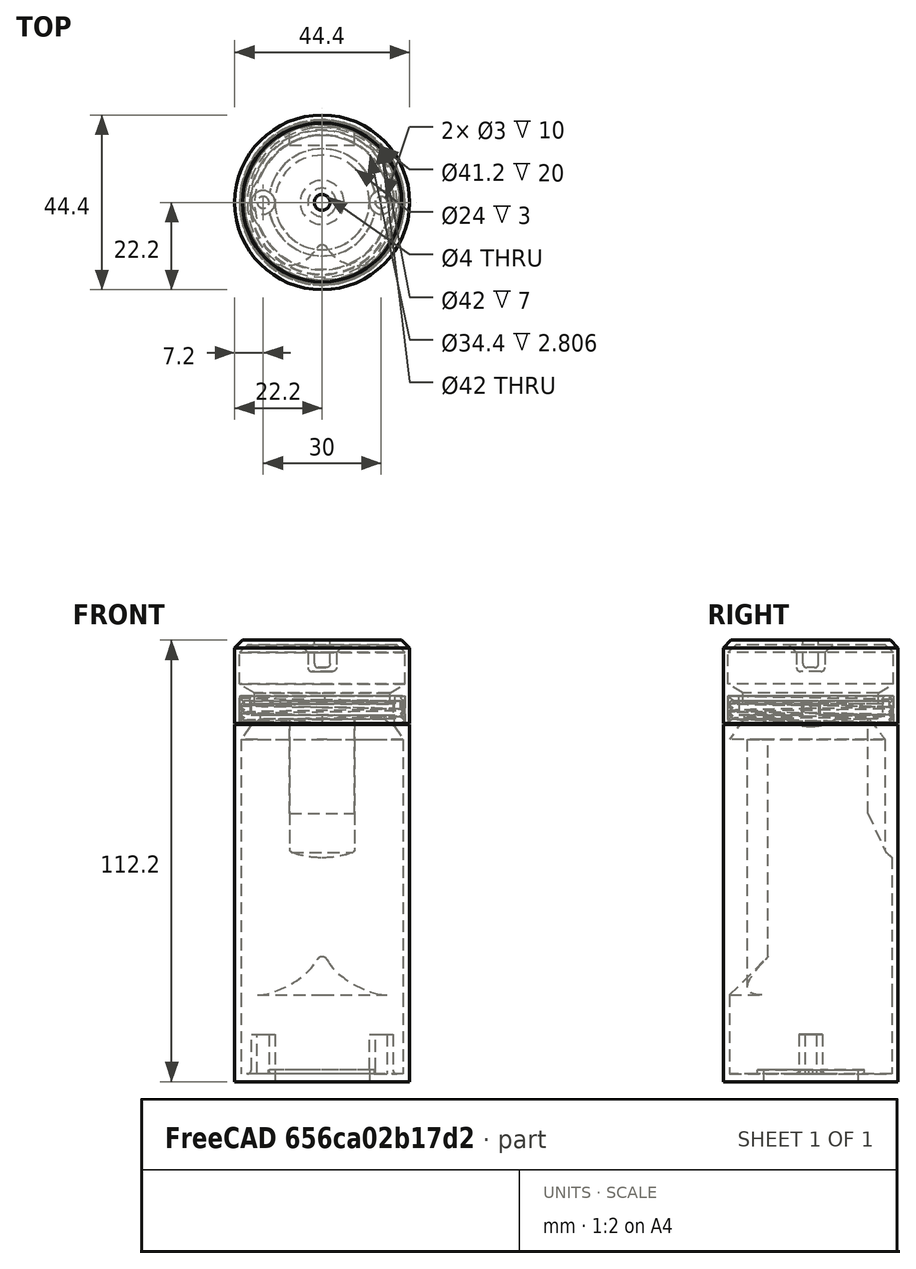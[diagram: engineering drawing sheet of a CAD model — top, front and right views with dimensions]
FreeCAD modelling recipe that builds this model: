
FCSTD DOCUMENT  (FreeCAD 0.20R29177 +426 (Git))
Label: base_case
License: All rights reserved
LicenseURL: http://en.wikipedia.org/wiki/All_rights_reserved
objects: Sketcher::SketchObject×10, PartDesign::Pad×3, PartDesign::Revolution×2, PartDesign::AdditiveHelix×2, PartDesign::Chamfer×2, PartDesign::Fillet×2, PartDesign::Pocket×2, PartDesign::Body×2, PartDesign::Plane×1, PartDesign::Groove×1
note: 41 computed .brp shape members not serialized (recipe doc carries the construction recipe); baked Part::Feature solids carry a one-line shape summary decoded from their .brp

FEATURE [Sketcher::SketchObject] Sketch
  FullyConstrained = true
  MapMode = 5
  Placement = pos=(0,0,0) rot=(1,0,0;1.5708rad)
  Support = -> [XZ_Plane]
  sketch-geometry (14):
    g0: LineSegment StartX=18.2 StartY=96.7788 StartZ=0 EndX=18.2 EndY=93.1788 EndZ=0
    g1: LineSegment StartX=18.2 StartY=93.1788 StartZ=0 EndX=17 EndY=93.1788 EndZ=0
    g2: LineSegment StartX=17 StartY=93.1788 StartZ=0 EndX=17 EndY=92.1788 EndZ=0
    g3: LineSegment StartX=17 StartY=92.1788 StartZ=0 EndX=20.6 EndY=87 EndZ=0
    g4: LineSegment StartX=20.6 StartY=87 StartZ=0 EndX=20.6 EndY=2 EndZ=0
    g5: LineSegment StartX=20.6 StartY=2 StartZ=0 EndX=13.6 EndY=2 EndZ=0
    g6: LineSegment StartX=13.6 StartY=2 StartZ=0 EndX=13.6 EndY=3 EndZ=0
    g7: LineSegment StartX=13.6 StartY=3 StartZ=0 EndX=12 EndY=3 EndZ=0
    g8: LineSegment StartX=12 StartY=3 StartZ=0 EndX=12 EndY=0 EndZ=0
    g9: LineSegment StartX=12 StartY=0 StartZ=0 EndX=22.2 EndY=0 EndZ=0
    g10: LineSegment StartX=19.8 StartY=96.7788 StartZ=0 EndX=18.2 EndY=96.7788 EndZ=0
    g11: LineSegment StartX=19.8 StartY=96.7788 StartZ=0 EndX=19.8 EndY=90.7788 EndZ=0
    g12: LineSegment StartX=19.8 StartY=90.7788 StartZ=0 EndX=22.2 EndY=90.7788 EndZ=0
    g13: LineSegment StartX=22.2 StartY=90.7788 StartZ=0 EndX=22.2 EndY=0 EndZ=0
  constraints (42):
    c: Vertical(g0)
    c: Coincident(g0,g1)
    c: Horizontal(g1)
    c: Coincident(g1,g2)
    c: Vertical(g2)
    c: Coincident(g2,g3)
    c: Coincident(g3,g4)
    c: Vertical(g4)
    c: Coincident(g4,g5)
    c: Horizontal(g5)
    c: Coincident(g5,g6)
    c: Vertical(g6)
    c: Coincident(g6,g7)
    c: Horizontal(g7)
    c: Coincident(g7,g8)
    c: PointOnObject(g8,g-1)
    c: Vertical(g8)
    c: Coincident(g8,g9)
    c: PointOnObject(g9,g-1)
    c: Coincident(g10,g0)
    c: Horizontal(g10)
    c: DistanceY(g2,g2) = 1
    c: DistanceX(g10,g10) = 1.6
    c: Equal(g7,g10)
    c: DistanceY(g8,g8) = 3
    c: DistanceY(g4,g4) = 85
    c: DistanceY(g6,g6) = 1
    c: DistanceX(g-1,g0) = 18.2
    c: Coincident(g10,g11)
    c: Vertical(g11)
    c: Coincident(g11,g12)
    c: Horizontal(g12)
    c: Coincident(g12,g13)
    c: Coincident(g13,g9)
    c: Vertical(g13)
    c: DistanceY(g11,g11) = 6
    c: DistanceX(g1,g1) = 1.2
    c: DistanceX(g4,g9) = 1.6
    c: DistanceY(g0,g0) = 3.6
    c: Distance(g11,g3) = 1.5
    c: DistanceX(g-1,g12) = 22.2
    c: DistanceX(g-1,g8) = 12
FEATURE [PartDesign::Revolution] Revolution  label="shell"
  Angle = 360
  Axis = (0,-2e-16,1)
  Base = (0,0,0)
  Placement = pos=(0,0,0) rot=(1,0,0;1.5708rad)
  Profile = -> Sketch
  ReferenceAxis = -> Sketch [V_Axis]
  Reversed = true
FEATURE [Sketcher::SketchObject] Sketch001
  ExternalGeometry = -> [Revolution]
  FullyConstrained = true
  MapMode = 5
  Placement = pos=(0,0,0) rot=(1,0,0;1.5708rad)
  Support = -> [XZ_Plane]
  sketch-geometry (4):
    g0: LineSegment StartX=20.8653 StartY=95.8596 StartZ=0 EndX=19.8 EndY=96.7788 EndZ=0
    g1: LineSegment StartX=19.8 StartY=96.7788 StartZ=0 EndX=19.8 EndY=94.7888 EndZ=0
    g2: LineSegment StartX=19.8 StartY=94.7888 StartZ=0 EndX=20.8653 EndY=95.7081 EndZ=0
    g3: ArcOfCircle CenterX=20.8 CenterY=95.7838 CenterZ=0 NormalX=0 NormalY=0 NormalZ=1 AngleXU=0 Radius=0.1 StartAngle=5.42433 EndAngle=7.14204
  constraints (10):
    c: Coincident(g0,g1)
    c: Coincident(g1,g2)
    c: Tangent(g0,g3) = -1.5708
    c: Tangent(g2,g3) = -1.5708
    c: Radius(g3) = 0.1
    c: DistanceY(g1,g1) = 1.99
    c: Equal(g2,g0)
    c: DistanceX(g0,g3) = 1
    c: Coincident(g0,g-3)
    c: PointOnObject(g1,g-3)
FEATURE [PartDesign::AdditiveHelix] AdditiveHelix  label="thread"
  Angle = 0
  Axis = (0,-2e-16,1)
  Base = (0,0,0)
  BaseFeature = -> Revolution
  Growth = 0
  HasBeenEdited = true
  Height = 6.5
  LeftHanded = false
  Mode = 0
  Outside = false
  Pitch = 2
  Placement = pos=(0,0,0) rot=(1,0,0;1.5708rad)
  Profile = -> Sketch001
  ReferenceAxis = -> Sketch001 [V_Axis]
  Reversed = true
  Turns = 3.25
FEATURE [Sketcher::SketchObject] Sketch002
  FullyConstrained = true
  MapMode = 5
  Placement = pos=(0,0,0) rot=(0.57735,0.57735,0.57735;2.0944rad)
  Support = -> [YZ_Plane001]
  sketch-geometry (17):
    g0: LineSegment StartX=18.4 StartY=98 StartZ=0 EndX=21 EndY=98 EndZ=0
    g1: LineSegment StartX=21 StartY=98 StartZ=0 EndX=21 EndY=91 EndZ=0
    g2: LineSegment StartX=21 StartY=91 StartZ=0 EndX=22.2 EndY=91 EndZ=0
    g3: LineSegment StartX=22.2 StartY=91 StartZ=0 EndX=22.2 EndY=112.2 EndZ=0
    g4: LineSegment StartX=2 StartY=112.2 StartZ=0 EndX=22.2 EndY=112.2 EndZ=0
    g5: LineSegment StartX=18.4 StartY=98 StartZ=0 EndX=18.4 EndY=96 EndZ=0
    g6: LineSegment StartX=18.4 StartY=96 StartZ=0 EndX=17.2 EndY=96 EndZ=0
    g7: LineSegment StartX=17.2 StartY=96 StartZ=0 EndX=17.2 EndY=98.8061 EndZ=0
    g8: LineSegment StartX=17.2 StartY=98.8061 StartZ=0 EndX=21 EndY=101 EndZ=0
    g9: LineSegment StartX=21 StartY=101 StartZ=0 EndX=21 EndY=111 EndZ=0
    g10: LineSegment StartX=21 StartY=111 StartZ=0 EndX=3.6 EndY=111 EndZ=0
    g11: LineSegment StartX=3.6 StartY=111 StartZ=0 EndX=3.6 EndY=104.2 EndZ=0
    g12: LineSegment StartX=3.6 StartY=104.2 StartZ=0 EndX=0 EndY=104.2 EndZ=0
    g13: LineSegment StartX=0 StartY=104.2 StartZ=0 EndX=0 EndY=105.2 EndZ=0
    g14: LineSegment StartX=0 StartY=105.2 StartZ=0 EndX=2 EndY=105.2 EndZ=0
    g15: LineSegment StartX=2 StartY=105.2 StartZ=0 EndX=2 EndY=112.2 EndZ=0
    g16: LineSegment StartX=21 StartY=101 StartZ=0 EndX=21 EndY=98 EndZ=0
  constraints (50):
    c: Horizontal(g0)
    c: Coincident(g0,g1)
    c: Vertical(g1)
    c: Coincident(g1,g2)
    c: Horizontal(g2)
    c: Coincident(g2,g3)
    c: Vertical(g3)
    c: DistanceX(g-1,g1) = 21
    c: Coincident(g4,g3)
    c: Horizontal(g4)
    c: DistanceY(g1,g1) = 7
    c: DistanceY(g-1,g2) = 91
    c: DistanceX(g2,g2) = 1.2
    c: Coincident(g5,g0)
    c: Coincident(g5,g6)
    c: Horizontal(g6)
    c: Coincident(g6,g7)
    c: Vertical(g7)
    c: Coincident(g7,g8)
    c: Coincident(g8,g9)
    c: Vertical(g9)
    c: Coincident(g9,g10)
    c: Horizontal(g10)
    c: Coincident(g10,g11)
    c: Coincident(g11,g12)
    c: PointOnObject(g12,g-2)
    c: Horizontal(g12)
    c: Coincident(g12,g13)
    c: PointOnObject(g13,g-2)
    c: Coincident(g13,g14)
    c: Horizontal(g14)
    c: Coincident(g14,g15)
    c: Vertical(g15)
    c: Coincident(g4,g15)
    c: Distance(g9,g4) = 1.2
    c: DistanceX(g14,g14) = 2
    c: Vertical(g5)
    c: DistanceY(g15,g15) = 7
    c: Distance(g14,g11) = 1.6
    c: Vertical(g11)
    c: DistanceY(g13,g13) = 1
    c: Coincident(g16,g8)
    c: Coincident(g16,g0)
    c: Vertical(g16)
    c: Angle(g9,g8) = 2.0944
    c: DistanceY(g5,g5) = 2
    c: DistanceX(g0,g0) = 2.6
    c: DistanceY(g9,g9) = 10
    c: DistanceX(g6,g6) = 1.2
    c: DistanceY(g16,g16) = 3
FEATURE [PartDesign::Revolution] Revolution001
  Angle = 360
  Axis = (-2e-16,3e-16,1)
  Base = (0,0,0)
  Placement = pos=(0,0,0) rot=(0.57735,0.57735,0.57735;2.0944rad)
  Profile = -> Sketch002
  ReferenceAxis = -> Sketch002 [V_Axis]
  Reversed = true
FEATURE [Sketcher::SketchObject] Sketch003
  ExternalGeometry = -> [Revolution001]
  FullyConstrained = true
  MapMode = 5
  Placement = pos=(0,0,0) rot=(0.57735,0.57735,0.57735;2.0944rad)
  Support = -> [YZ_Plane001]
  sketch-geometry (4):
    g0: LineSegment StartX=19.9347 StartY=91.9193 StartZ=0 EndX=21 EndY=91 EndZ=0
    g1: LineSegment StartX=21 StartY=92.99 StartZ=0 EndX=19.9347 EndY=92.0707 EndZ=0
    g2: ArcOfCircle CenterX=20 CenterY=91.995 CenterZ=0 NormalX=0 NormalY=0 NormalZ=1 AngleXU=0 Radius=0.1 StartAngle=2.28274 EndAngle=4.00044
    g3: LineSegment StartX=21 StartY=92.99 StartZ=0 EndX=21 EndY=91 EndZ=0
  constraints (10):
    c: Coincident(g0,g-3)
    c: PointOnObject(g1,g-3)
    c: Equal(g1,g0)
    c: DistanceY(g0,g1) = 1.99
    c: Tangent(g0,g2) = -1.5708
    c: Tangent(g1,g2) = -1.5708
    c: DistanceX(g2,g1) = 1
    c: Radius(g2) = 0.1
    c: Coincident(g3,g1)
    c: Coincident(g3,g0)
FEATURE [PartDesign::AdditiveHelix] AdditiveHelix001
  Angle = 0
  Axis = (-2e-16,3e-16,1)
  Base = (0,0,0)
  BaseFeature = -> Revolution001
  Growth = 0
  HasBeenEdited = true
  Height = 5.99
  LeftHanded = false
  Mode = 0
  Outside = false
  Pitch = 2
  Placement = pos=(0,0,0) rot=(0.57735,0.57735,0.57735;2.0944rad)
  Profile = -> Sketch003
  ReferenceAxis = -> Sketch003 [V_Axis]
  Turns = 2.995
FEATURE [PartDesign::Chamfer] Chamfer
  Angle = 45
  Base = -> AdditiveHelix001 [Edge50,Edge52,Edge31]
  BaseFeature = -> AdditiveHelix001
  ChamferType = 0
  FlipDirection = false
  Placement = pos=(0,0,0) rot=(0.57735,0.57735,0.57735;2.0944rad)
  Size = 2
  Size2 = 1
  SupportTransform = false
  UseAllEdges = false
FEATURE [Sketcher::SketchObject] Sketch004
  ExternalGeometry = -> [AdditiveHelix]
  FullyConstrained = true
  MapMode = 5
  Placement = pos=(0,0,0) rot=(0.57735,0.57735,0.57735;2.0944rad)
  Support = -> [YZ_Plane]
  sketch-geometry (5):
    g0: LineSegment StartX=14.5 StartY=92.1788 StartZ=0 EndX=17 EndY=92.1788 EndZ=0
    g1: LineSegment StartX=17 StartY=92.1788 StartZ=0 EndX=20.6 EndY=87 EndZ=0
    g2: LineSegment StartX=20.6 StartY=87 StartZ=0 EndX=20.6 EndY=57 EndZ=0
    g3: LineSegment StartX=20.6 StartY=57 StartZ=0 EndX=14.5 EndY=62.1788 EndZ=0
    g4: LineSegment StartX=14.5 StartY=62.1788 StartZ=0 EndX=14.5 EndY=92.1788 EndZ=0
  constraints (13):
    c: Coincident(g0,g1)
    c: Coincident(g1,g2)
    c: Vertical(g2)
    c: Coincident(g2,g3)
    c: Coincident(g3,g4)
    c: Vertical(g4)
    c: Coincident(g4,g0)
    c: DistanceX(g0,g0) = 2.5
    c: DistanceY(g4,g4) = 30
    c: DistanceY(g2,g2) = 30
    c: Coincident(g1,g-3)
    c: Coincident(g0,g-4)
    c: PointOnObject(g0,g-4)
FEATURE [PartDesign::Pad] Pad  label="charger mount"
  BaseFeature = -> AdditiveHelix
  Direction = (1,-2e-16,3e-16)
  Length = 16.49
  Length2 = 10
  Midplane = true
  Placement = pos=(0,0,0) rot=(1,0,0;1.5708rad)
  Profile = -> Sketch004
  ReferenceAxis = -> Sketch004 [N_Axis]
  Type = 0
FEATURE [PartDesign::Plane] DatumPlane
  Length = 60
  MapMode = 11
  Placement = pos=(0,1.93e-14,87) rot=(0.707107,-0.707107,0;3.14159rad)
  ResizeMode = 0
  Support = -> [Pad]
  Width = 60
FEATURE [Sketcher::SketchObject] Sketch005
  ExternalGeometry = -> [Pad]
  FullyConstrained = true
  MapMode = 5
  Placement = pos=(0,1.93e-14,87) rot=(0,0,1;1.5708rad)
  Support = -> [DatumPlane]
  sketch-geometry (4):
    g0: ArcOfCircle CenterX=3e-16 CenterY=0 CenterZ=0 NormalX=0 NormalY=0 NormalZ=1 AngleXU=0 Radius=20.6 StartAngle=2.21575 EndAngle=4.06743
    g1: ArcOfCircle CenterX=-6.88331 CenterY=9.15 CenterZ=0 NormalX=0 NormalY=0 NormalZ=1 AngleXU=0 Radius=9.15 StartAngle=2.21575 EndAngle=4.17521
    g2: ArcOfCircle CenterX=-6.88331 CenterY=-9.15 CenterZ=0 NormalX=0 NormalY=0 NormalZ=1 AngleXU=0 Radius=9.15 StartAngle=2.10798 EndAngle=4.06743
    g3: ArcOfCircle CenterX=-12.3331 CenterY=0 CenterZ=0 NormalX=0 NormalY=0 NormalZ=1 AngleXU=0 Radius=1.5 StartAngle=5.24957 EndAngle=7.3168
  constraints (11):
    c: Coincident(g0,g-3)
    c: PointOnObject(g0,g-3)
    c: Tangent(g1,g0) = -1.5708
    c: Tangent(g2,g0) = -1.5708
    c: Equal(g2,g1)
    c: Diameter(g2) = 18.3
    c: Tangent(g1,g3) = 1.5708
    c: Tangent(g2,g3) = 1.5708
    c: Radius(g3) = 1.5
    c: PointOnObject(g3,g-1)
    c: Distance(g2,g1) = 18.3
FEATURE [PartDesign::Pad] Pad001  label="18650 slots"
  BaseFeature = -> Pad
  Direction = (0,2e-16,1)
  Length = 65
  Length2 = 10
  Placement = pos=(0,0,0) rot=(1,0,0;1.5708rad)
  Profile = -> Sketch005
  ReferenceAxis = -> Sketch005 [N_Axis]
  Reversed = true
  Type = 0
FEATURE [Sketcher::SketchObject] Sketch006
  ExternalGeometry = -> [Pad001]
  FullyConstrained = true
  MapMode = 5
  Placement = pos=(0,7e-16,2) rot=(0,0,1;3.14159rad)
  Support = -> [Pad001]
  sketch-geometry (4):
    g0: Circle CenterX=15 CenterY=0 CenterZ=0 NormalX=0 NormalY=0 NormalZ=1 AngleXU=0 Radius=1.5
    g1: Circle CenterX=-15 CenterY=0 CenterZ=0 NormalX=0 NormalY=0 NormalZ=1 AngleXU=0 Radius=1.5
    g2: Circle CenterX=15 CenterY=0 CenterZ=0 NormalX=0 NormalY=0 NormalZ=1 AngleXU=0 Radius=3
    g3: Circle CenterX=-15 CenterY=0 CenterZ=0 NormalX=0 NormalY=0 NormalZ=1 AngleXU=0 Radius=3
  constraints (9):
    c: PointOnObject(g0,g-1)
    c: Coincident(g2,g0)
    c: Tangent(g2,g-3)
    c: Coincident(g3,g1)
    c: Tangent(g3,g-3)
    c: Equal(g1,g0)
    c: Diameter(g1) = 3
    c: DistanceX(g1,g0) = 30
    c: Symmetric(g0,g1,g-3)
FEATURE [PartDesign::Pad] Pad002
  BaseFeature = -> Pad001
  Direction = (0,3e-16,1)
  Length = 10
  Length2 = 10
  Placement = pos=(0,0,0) rot=(1,0,0;1.5708rad)
  Profile = -> Sketch006
  ReferenceAxis = -> Sketch006 [N_Axis]
  Type = 0
FEATURE [PartDesign::Chamfer] Chamfer001
  Angle = 45
  Base = -> Pad002 [Edge57]
  BaseFeature = -> Pad002
  ChamferType = 0
  FlipDirection = false
  Placement = pos=(0,0,0) rot=(1,0,0;1.5708rad)
  Size = 6
  Size2 = 1
  SupportTransform = false
  UseAllEdges = false
FEATURE [PartDesign::Fillet] Fillet
  Base = -> Chamfer001 [Edge26,Edge28]
  BaseFeature = -> Chamfer001
  Placement = pos=(0,0,0) rot=(1,0,0;1.5708rad)
  Radius = 1
  SupportTransform = false
  UseAllEdges = false
FEATURE [Sketcher::SketchObject] Sketch007
  FullyConstrained = true
  MapMode = 5
  Placement = pos=(0,4.3e-14,96.7788) rot=(0,0,1;3.14159rad)
  Support = -> [Fillet]
  sketch-geometry (1):
    g0: Circle CenterX=9.15 CenterY=0 CenterZ=0 NormalX=0 NormalY=0 NormalZ=1 AngleXU=0 Radius=9.15
  constraints (3):
    c: PointOnObject(g0,g-1)
    c: PointOnObject(g-1,g0)
    c: Diameter(g0) = 18.3
FEATURE [PartDesign::Pocket] Pocket
  BaseFeature = -> Fillet
  Direction = (0,-4e-16,-1)
  Length = 8
  Length2 = 5
  Placement = pos=(0,0,0) rot=(1,0,0;1.5708rad)
  Profile = -> Sketch007
  ReferenceAxis = -> Sketch007 [N_Axis]
  Type = 0
FEATURE [Sketcher::SketchObject] Sketch008
  FullyConstrained = true
  MapMode = 5
  Placement = pos=(0,5.37e-14,96.7788) rot=(0,0,1;3.14159rad)
  Support = -> [Pocket]
  sketch-geometry (1):
    g0: Circle CenterX=-9.175 CenterY=0 CenterZ=0 NormalX=0 NormalY=0 NormalZ=1 AngleXU=0 Radius=9.175
  constraints (3):
    c: PointOnObject(g0,g-1)
    c: PointOnObject(g-1,g0)
    c: Diameter(g0) = 18.35
FEATURE [PartDesign::Pocket] Pocket001
  BaseFeature = -> Pocket
  Direction = (0,-6e-16,-1)
  Length = 7
  Length2 = 5
  Placement = pos=(0,0,0) rot=(1,0,0;1.5708rad)
  Profile = -> Sketch008
  ReferenceAxis = -> Sketch008 [N_Axis]
  Type = 0
FEATURE [Sketcher::SketchObject] Sketch009
  ExternalGeometry = -> [Pocket001]
  FullyConstrained = true
  MapMode = 5
  Placement = pos=(0,0,0) rot=(0.57735,0.57735,0.57735;2.0944rad)
  Support = -> [YZ_Plane]
  sketch-geometry (3):
    g0: LineSegment StartX=-20.6 StartY=22 StartZ=0 EndX=-10.5655 EndY=32.0345 EndZ=0
    g1: LineSegment StartX=-10.5655 StartY=32.0345 StartZ=0 EndX=-10.5655 EndY=22 EndZ=0
    g2: LineSegment StartX=-10.5655 StartY=22 StartZ=0 EndX=-20.6 EndY=22 EndZ=0
  constraints (8):
    c: Coincident(g-3,g0)
    c: Coincident(g0,g1)
    c: Vertical(g1)
    c: Coincident(g1,g2)
    c: Coincident(g2,g0)
    c: Horizontal(g2)
    c: Distance(g0,g-4) = 1
    c: Angle(g2,g0) = 0.785398
FEATURE [PartDesign::Groove] Groove
  Angle = 360
  Axis = (-2e-16,3e-16,1)
  Base = (0,0,0)
  BaseFeature = -> Pocket001
  Placement = pos=(0,0,0) rot=(1,0,0;1.5708rad)
  Profile = -> Sketch009
  ReferenceAxis = -> Sketch009 [V_Axis]
  Reversed = true
FEATURE [PartDesign::Body] Body  label="case"
  Group = -> [Sketch,Revolution,Sketch001,AdditiveHelix,Sketch004,Pad,DatumPlane,Sketch005,Pad001,Sketch006,Pad002,Chamfer001,Fillet,Sketch007,Pocket,Sketch008,Pocket001,Sketch009,Groove]
  Origin = -> Origin
  Tip = -> Groove
FEATURE [PartDesign::Fillet] Fillet001
  Base = -> Chamfer [Edge60,Edge13]
  BaseFeature = -> Chamfer
  Placement = pos=(0,0,0) rot=(0.57735,0.57735,0.57735;2.0944rad)
  Radius = 1
  SupportTransform = false
  UseAllEdges = false
FEATURE [PartDesign::Body] Body001  label="Lid"
  Group = -> [Sketch002,Revolution001,Sketch003,AdditiveHelix001,Chamfer,Fillet001]
  Origin = -> Origin001
  Tip = -> Fillet001
